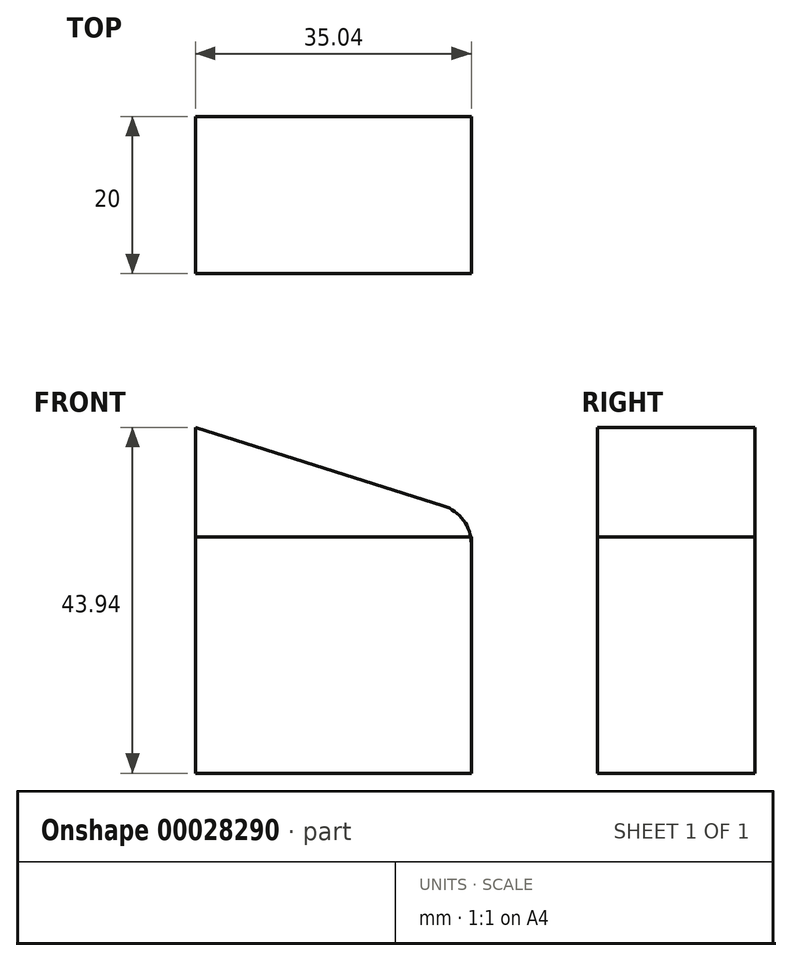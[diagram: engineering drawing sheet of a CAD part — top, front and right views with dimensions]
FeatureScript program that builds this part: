
annotation { "Feature Type Name" : "Feature", "Feature Type Description" : "" }
export const myFeature = defineFeature(function(context is Context, id is Id, definition is map)
    precondition{}
    {
        {
            var Q0;
            Q0=qCreatedBy(makeId("Front.planeOp"),FACE);
            var sketch = newSketch(context, id + "F0", { "sketchPlane" : qUnion([Q0])});
            skLineSegment(sketch, "E0", {"start": v(0, 0) * mm, "end": v(35.04, 0) * mm});
            skLineSegment(sketch, "E1", {"start": v(35.04, 0) * mm, "end": v(35.04, 32.85) * mm});
            skLineSegment(sketch, "E2", {"start": v(35.04, 32.85) * mm, "end": v(0, 43.94) * mm});
            skLineSegment(sketch, "E3", {"start": v(0, 0) * mm, "end": v(0, 43.94) * mm});
            skSolve(sketch);
        }
        {
            var Q0;
            Q0=makeQuery(id+"F0.imprint","IMPRINT",FACE,{"disambiguationData":[TD([[makeQuery(id+"F0.imprint","IMPRINT",EDGE,{"derivedFrom":sQuery(id+"F0.wireOp",EDGE,"E0")}),1.0]])]});
            extrude(context, id + "F1", {"entities" : qUnion([Q0]), "oppositeDirection" : true, "depth" : 20 * mm});
        }
        {
            var Q0;
            Q0=makeQuery(id+"F1.opExtrude","SWEPT_EDGE",EDGE,{"disambiguationData":[OSD([sQuery(id+"F0.wireOp",EDGE,"E1"),sQuery(id+"F0.wireOp",EDGE,"E2")])]});
            fillet(context, id + "F2", {"entities" : qUnion([Q0]), "radius" : 5.08 * mm, "tangentPropagation" : true, "allowEdgeOverflow" : false});
        }
        {
            var Q0;
            {var subQ0=sQuery(id+"F0.wireOp",EDGE,"E0");var subQ1=sQuery(id+"F0.wireOp",EDGE,"E1");var subQ2=sQuery(id+"F0.wireOp",EDGE,"E2");var subQ3=sQuery(id+"F0.wireOp",EDGE,"E3");Q0=makeQuery(id+"F1WbjmxPqo7s8GQ_1.opShell","OFFSET_FACE",FACE,{"disambiguationData":[OSD([subQ0,subQ1,subQ2,subQ3]),TDD([makeQuery(id+"F1.opExtrude","CAP_FACE",FACE,{"disambiguationData":[OSD([subQ0,subQ1,subQ2,subQ3])],"isStart":true})])]});}
            var Q1;
            Q1=makeQuery(id+"F1WbjmxPqo7s8GQ_1.opShell","OFFSET_FACE",FACE,{"disambiguationData":[OSD([sQuery(id+"F0.wireOp",EDGE,"E0")])]});
            var Q2;
            Q2=makeQuery(id+"F1.opExtrude","SWEPT_FACE",FACE,{"disambiguationData":[OSD([sQuery(id+"F0.wireOp",EDGE,"E0")])]});
            extrude(context, id + "F3", {"entities" : qUnion([Q0, Q1, Q2]), "oppositeDirection" : true, "depth" : 30 * mm});
        }
    });
